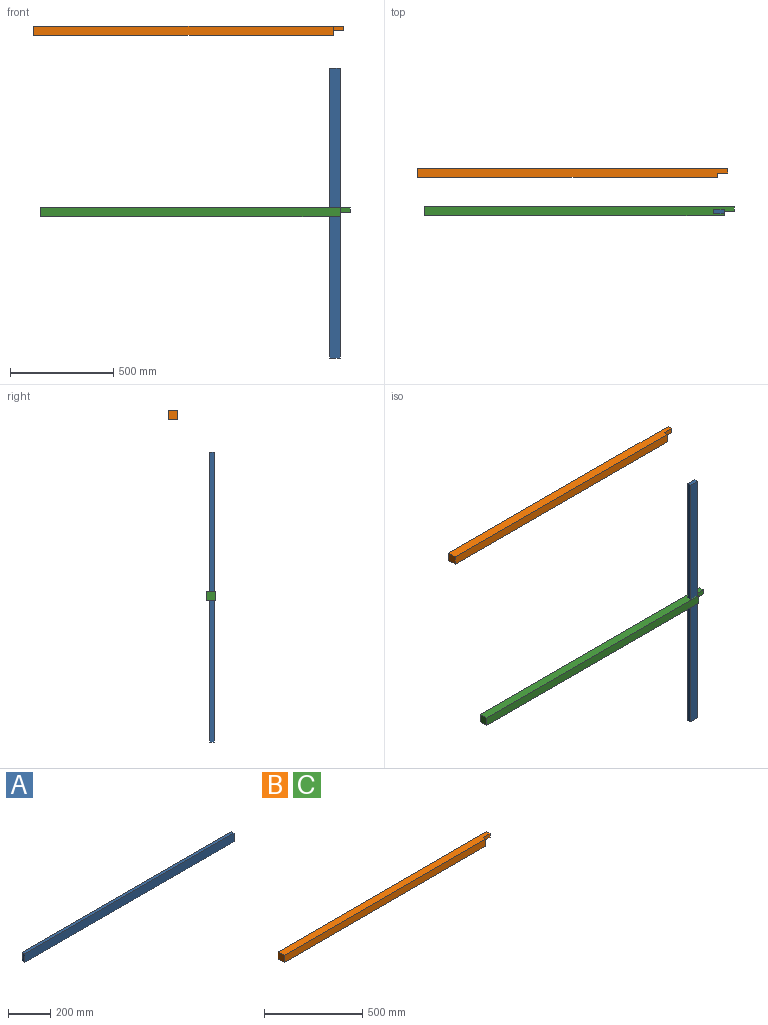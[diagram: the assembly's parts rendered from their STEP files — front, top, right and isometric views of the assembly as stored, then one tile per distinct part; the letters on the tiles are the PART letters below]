
ASSEMBLY  parts=3 mates=2
PART A: 6 faces, bbox 1400x20x50 mm
  f0: plane 50x20mm, normal (-1,0,0), area 1000mm2, adj f1,f3,f4,f5
  f1: plane 1400x20mm, normal (0,0,-1), area 28000mm2, adj f0,f2,f4,f5
  f2: plane 50x20mm, normal (1,0,0), area 1000mm2, adj f1,f3,f4,f5
  f3: plane 1400x20mm, normal (0,0,1), area 28000mm2, adj f0,f2,f4,f5
  f4: plane 1400x50mm, normal (0,-1,0), area 70000mm2, adj f0,f1,f2,f3
  f5: plane 1400x50mm, normal (0,1,0), area 70000mm2, adj f0,f1,f2,f3
PART B: 9 faces, bbox 1500x44x44 mm
  f0: plane 1450x44mm, normal (0,0,-1), area 63800mm2, adj f1,f3,f4,f8
  f1: plane 1450x44mm, normal (0,-1,0), area 63800mm2, adj f0,f2,f4,f8
  f2: plane 1500x44mm, normal (0,0,1), area 65000mm2, adj f1,f3,f4,f5,f6,f8
  f3: plane 1500x44mm, normal (0,1,0), area 65000mm2, adj f0,f2,f4,f5,f7,f8
  f4: plane 44x44mm, normal (-1,0,0), area 1936mm2, adj f0,f1,f2,f3
  f5: plane 24x24mm, normal (1,0,0), area 576mm2, adj f2,f3,f6,f7
  f6: plane 50x24mm, normal (0,-1,0), area 1200mm2, adj f2,f5,f7,f8
  f7: plane 50x24mm, normal (0,0,-1), area 1200mm2, adj f3,f5,f6,f8
  f8: plane 44x44mm, normal (1,0,0), area 1360mm2, adj f0,f1,f2,f3,f6,f7
PART C: same geometry as B
PLACE A rot(axis=(0.71,0,-0.71),180deg) t=(1103.1,-202.36,710.74)mm
PLACE B t=(-379.24,18.69,694.75)mm
PLACE C t=(-346.9,-166.12,-184.37)mm
MATE parallel A.f1 <-> C.f8  axis (1,0,0) through (1103.1,-192.36,10.74)mm
MATE parallel B.f8 <-> C.f8  axis (1,0,0) through (1070.76,-7.55,889.86)mm
